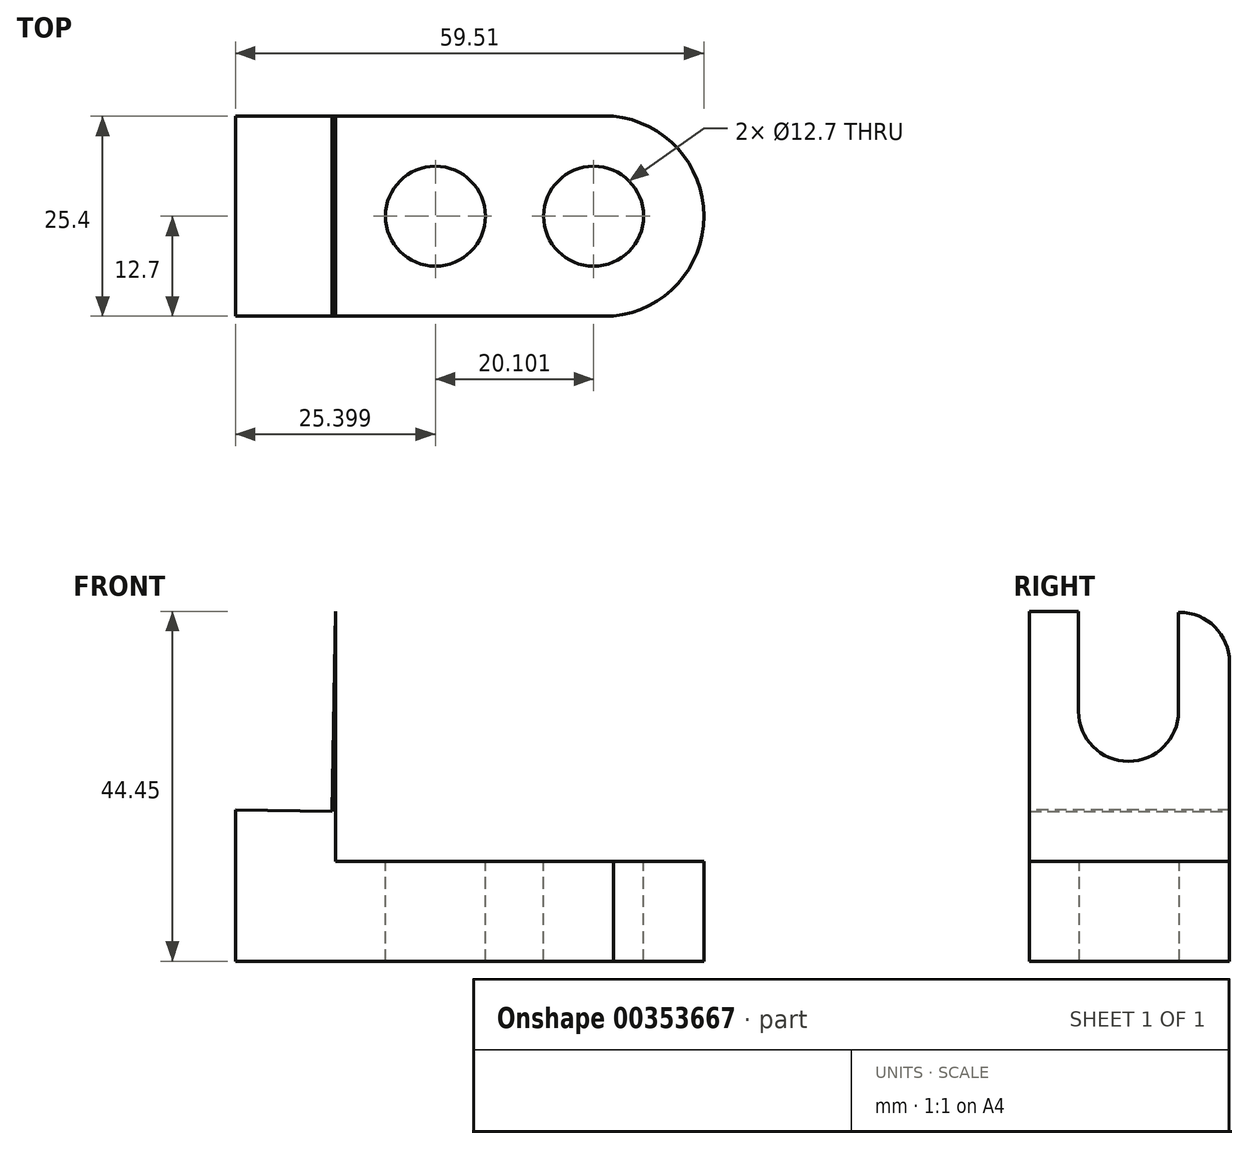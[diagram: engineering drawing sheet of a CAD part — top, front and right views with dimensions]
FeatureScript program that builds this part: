
annotation { "Feature Type Name" : "Feature", "Feature Type Description" : "" }
export const myFeature = defineFeature(function(context is Context, id is Id, definition is map)
    precondition{}
    {
        {
            var Q0;
            Q0=qCreatedBy(makeId("Front.planeOp"),FACE);
            var sketch = newSketch(context, id + "F0", { "sketchPlane" : qUnion([Q0])});
            skLineSegment(sketch, "E0", {"start": v(-45.5, 44.66) * mm, "end": v(-45.5, 0) * mm});
            skLineSegment(sketch, "E1", {"start": v(-45.5, 0) * mm, "end": v(30.7, 0) * mm});
            skLineSegment(sketch, "E2", {"start": v(30.7, 0) * mm, "end": v(30.7, 12.7) * mm});
            skLineSegment(sketch, "E3", {"start": v(30.7, 12.7) * mm, "end": v(-32.8, 12.7) * mm});
            skLineSegment(sketch, "E4", {"start": v(-32.8, 12.7) * mm, "end": v(-32.8, 44.45) * mm});
            skLineSegment(sketch, "E5", {"start": v(-32.8, 44.45) * mm, "end": v(-45.5, 44.66) * mm});
            skSolve(sketch);
        }
        {
            var Q0;
            Q0 = qSketchRegion(id + "F0", true);
            extrude(context, id + "F1", {"entities" : qUnion([Q0]), "depth" : 25.4 * mm});
        }
        {
            var Q0;
            Q0=makeQuery(id+"F1.opExtrude","SWEPT_FACE",FACE,{"disambiguationData":[OSD([sQuery(id+"F0.wireOp",EDGE,"E3")])]});
            var sketch = newSketch(context, id + "F2", { "sketchPlane" : qUnion([Q0])});
            skCircle(sketch, "E6", {"center": v(-20.1, -12.7) * mm, "radius": 6.35 * mm});
            skCircle(sketch, "E7", {"center": v(0, -12.7) * mm, "radius": 6.35 * mm});
            skArc(sketch, "E8", {"start": v(0, -25.4) * mm, "mid": v(14, -12.7) * mm, "end": v(0, 0) * mm});
            skSolve(sketch);
        }
        {
            var Q0;
            Q0 = qSketchRegion(id + "F2", true);
            var Q1;
            {var subQ1=sQuery(id+"F0.wireOp",EDGE,"E3");var subQ6=makeQuery(id+"F1.opExtrude","SWEPT_EDGE",EDGE,{"disambiguationData":[OSD([sQuery(id+"F0.wireOp",EDGE,"E2"),subQ1])]});Q1=makeQuery(id+"F2.imprint","IMPRINT",FACE,{"disambiguationData":[TD([[makeQuery(id+"F2.imprint","IMPRINT",EDGE,{"derivedFrom":subQ6}),1.0]])]});}
            extrude(context, id + "F3", {"entities" : qUnion([Q0, Q1]), "operationType" : NewBodyOperationType.REMOVE, "oppositeDirection" : true, "depth" : 25.4 * mm});
        }
        {
            var Q0;
            Q0=makeQuery(id+"F1.opExtrude","SWEPT_FACE",FACE,{"disambiguationData":[OSD([sQuery(id+"F0.wireOp",EDGE,"E4")])]});
            var sketch = newSketch(context, id + "F4", { "sketchPlane" : qUnion([Q0])});
            skPoint(sketch, "E9.startSnap0", {"position": v(0, 28.57) * mm});
            skCircle(sketch, "E10", {"center": v(-12.83, 31.75) * mm, "radius": 6.35 * mm});
            skLineSegment(sketch, "E11", {"start": v(-19.18, 31.75) * mm, "end": v(-19.18, 44.45) * mm});
            skLineSegment(sketch, "E12", {"start": v(-6.48, 31.75) * mm, "end": v(-6.48, 44.45) * mm});
            skSolve(sketch);
        }
        {
            var Q0;
            Q0 = qSketchRegion(id + "F4", true);
            var Q1;
            {var subQ0=sQuery(id+"F4.wireOp",EDGE,"E11");Q1=makeQuery(id+"F4.imprint","IMPRINT",FACE,{"disambiguationData":[TD([[makeQuery(id+"F4.imprint","IMPRINT",EDGE,{"derivedFrom":subQ0}),-1.0]])]});}
            extrude(context, id + "F5", {"entities" : qUnion([Q0, Q1]), "operationType" : NewBodyOperationType.REMOVE, "oppositeDirection" : true, "depth" : 25.4 * mm});
        }
        {
            var Q0;
            Q0=makeQuery(id+"F1.opExtrude","SWEPT_FACE",FACE,{"disambiguationData":[OSD([sQuery(id+"F0.wireOp",EDGE,"E4")])]});
            var sketch = newSketch(context, id + "F6", { "sketchPlane" : qUnion([Q0])});
            skLineSegment(sketch, "E13", {"start": v(-19.05, 44.45) * mm, "end": v(-19.18, 44.45) * mm});
            skLineSegment(sketch, "E14", {"start": v(-25.4, 38.1) * mm, "end": v(-25.4, 12.7) * mm});
            skPoint(sketch, "E15.visualSharp", {"position": v(-25.4, 44.45) * mm});
            skArc(sketch, "E15.filletArc", {"start": v(-19.05, 44.45) * mm, "mid": v(-23.54, 42.6) * mm, "end": v(-25.4, 38.1) * mm});
            skSolve(sketch);
        }
        {
            var Q0;
            {var subQ3=sQuery(id+"F6.wireOp",EDGE,"E14");Q0=makeQuery(id+"F6.imprint","IMPRINT",FACE,{"disambiguationData":[TD([[makeQuery(id+"F6.imprint","IMPRINT",EDGE,{"derivedFrom":subQ3}),-1.0]])]});}
            var sketch = newSketch(context, id + "F7", { "sketchPlane" : qUnion([Q0])});
            skLineSegment(sketch, "E16", {"start": v(-6.55, 44.34) * mm, "end": v(-6.35, 44.34) * mm});
            skLineSegment(sketch, "E17", {"start": v(0, 37.99) * mm, "end": v(0, 13.06) * mm});
            skPoint(sketch, "E18.visualSharp", {"position": v(0, 44.34) * mm});
            skArc(sketch, "E18.filletArc", {"start": v(0, 37.99) * mm, "mid": v(-1.86, 42.48) * mm, "end": v(-6.35, 44.34) * mm});
            skSolve(sketch);
        }
        {
            var Q0;
            {var subQ0=sQuery(id+"F6.wireOp",EDGE,"E15.filletArc");var subQ4=sQuery(id+"F4.wireOp",EDGE,"E11");var subQ5=makeQuery(id+"F5.boolean.opBoolean","COPY",EDGE,{"derivedFrom":makeQuery(id+"F5.opExtrude","CAP_EDGE",EDGE,{"disambiguationData":[OSD([subQ4])],"isStart":true})});var subQ6=makeQuery(id+"F6.imprint","INTERSECT",VERTEX,{"derivedFrom":[subQ5,subQ0]});Q0=makeQuery(id+"F6.imprint","IMPRINT",FACE,{"disambiguationData":[TD([[makeQuery(id+"F6.imprint","IMPRINT",EDGE,{"disambiguationData":[TD([[subQ6,-1.0]])],"derivedFrom":subQ0}),-1.0]])]});}
            var Q1;
            {var subQ4=sQuery(id+"F7.wireOp",EDGE,"E18.filletArc");Q1=makeQuery(id+"F7.imprint","IMPRINT",FACE,{"disambiguationData":[TD([[makeQuery(id+"F7.imprint","IMPRINT",EDGE,{"derivedFrom":subQ4}),-1.0]])]});}
            extrude(context, id + "F8", {"entities" : qUnion([Q0, Q1]), "operationType" : NewBodyOperationType.REMOVE, "oppositeDirection" : true, "depth" : 25.4 * mm});
        }
        {
            var Q0;
            Q0=makeQuery(id+"F1.opExtrude","SWEPT_FACE",FACE,{"disambiguationData":[OSD([sQuery(id+"F0.wireOp",EDGE,"E5")])]});
            var sketch = newSketch(context, id + "F9", { "sketchPlane" : qUnion([Q0])});
            skLineSegment(sketch, "E19", {"start": v(-46.22, 0) * mm, "end": v(-33.52, 0) * mm});
            skLineSegment(sketch, "E20", {"start": v(-33.52, 0) * mm, "end": v(-33.52, -25.4) * mm});
            skLineSegment(sketch, "E21", {"start": v(-33.52, -25.4) * mm, "end": v(-46.22, -25.4) * mm});
            skLineSegment(sketch, "E22", {"start": v(-46.22, -25.4) * mm, "end": v(-46.22, 0) * mm});
            skSolve(sketch);
        }
        {
            var Q0;
            Q0 = qSketchRegion(id + "F9", true);
            extrude(context, id + "F10", {"entities" : qUnion([Q0]), "operationType" : NewBodyOperationType.REMOVE, "oppositeDirection" : true, "depth" : 25.4 * mm});
        }
    });
